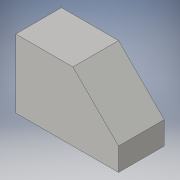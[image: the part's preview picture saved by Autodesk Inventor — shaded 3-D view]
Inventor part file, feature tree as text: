
AUTODESK INVENTOR PART (.ipt)
format: ipt  version: 2016 (Build 200138000, 138)  size: 92,160 bytes
history: native  units: in
note: dims shown in document units (in); Inventor stores cm internally (conversion verified against a paired STEP export)
features: extrude x1, chamfer x1, sketch x1
ambient origin geometry x8: Origin, YZ Plane, XZ Plane, XY Plane, X Axis, Y Axis, Z Axis, Center Point
bodies: Solid1 (feature_tree)
feature tree (3):
  extrude  "Extrusion1"  Depth=1.5in
  chamfer  "Chamfer1"  Distance=1.0in
  sketch  "Sketch1"  dims[d0=2.25in d1=1.5in d2=1.0in d3=0.0in d4=1.0in d5=0.125in d6=45.0deg]
